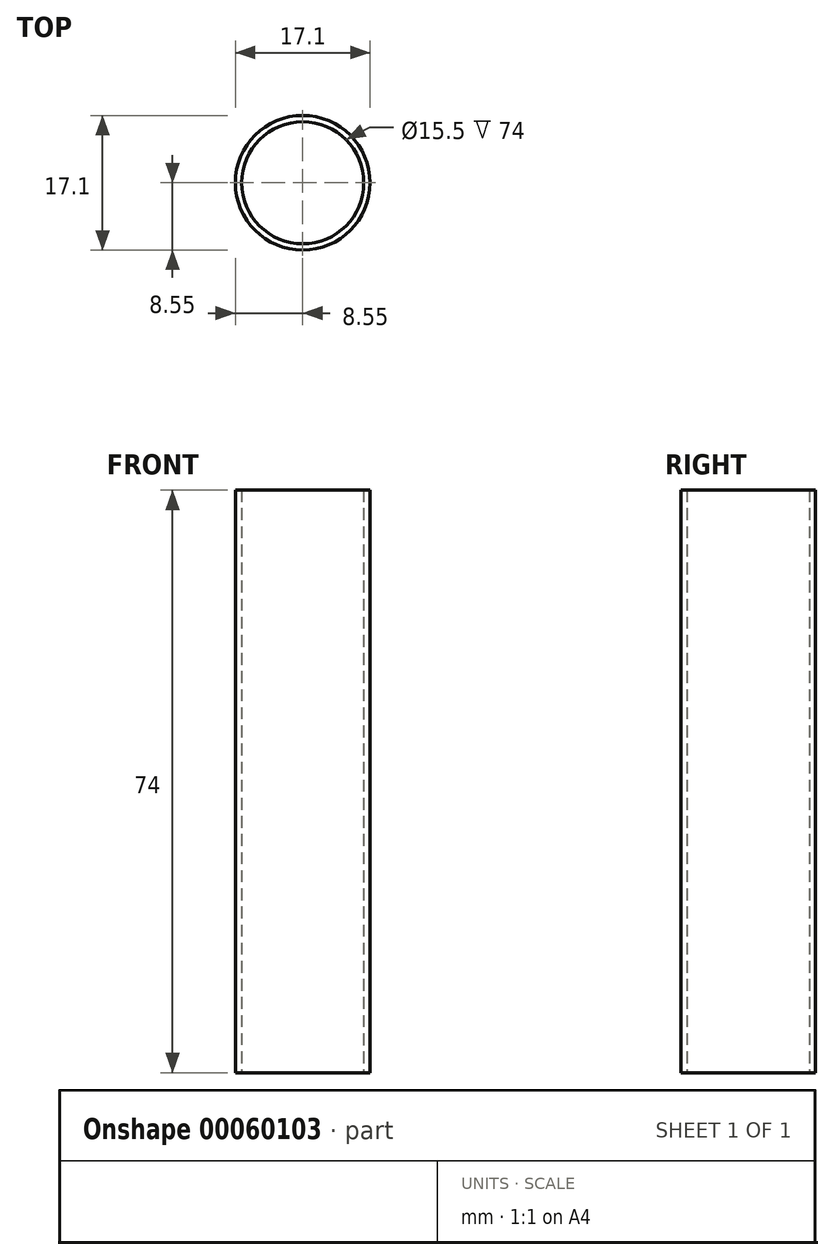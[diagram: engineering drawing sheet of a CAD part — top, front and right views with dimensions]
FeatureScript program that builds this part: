
annotation { "Feature Type Name" : "Feature", "Feature Type Description" : "" }
export const myFeature = defineFeature(function(context is Context, id is Id, definition is map)
    precondition{}
    {
        {
            var Q0;
            Q0=qCreatedBy(makeId("Top.planeOp"),FACE);
            var sketch = newSketch(context, id + "F0", { "sketchPlane" : qUnion([Q0])});
            skCircle(sketch, "E0", {"center": v(0, 0) * mm, "radius": 7.75 * mm});
            skCircle(sketch, "E1", {"center": v(0, 0) * mm, "radius": 8.55 * mm});
            skSolve(sketch);
        }
        {
            var Q0;
            Q0=makeQuery(id+"F0.imprint","IMPRINT",FACE,{"disambiguationData":[TD([[makeQuery(id+"F0.imprint","IMPRINT",EDGE,{"derivedFrom":sQuery(id+"F0.wireOp",EDGE,"E0")}),-1.0]])]});
            extrude(context, id + "F1", {"entities" : qUnion([Q0]), "depth" : 74 * mm});
        }
    });
